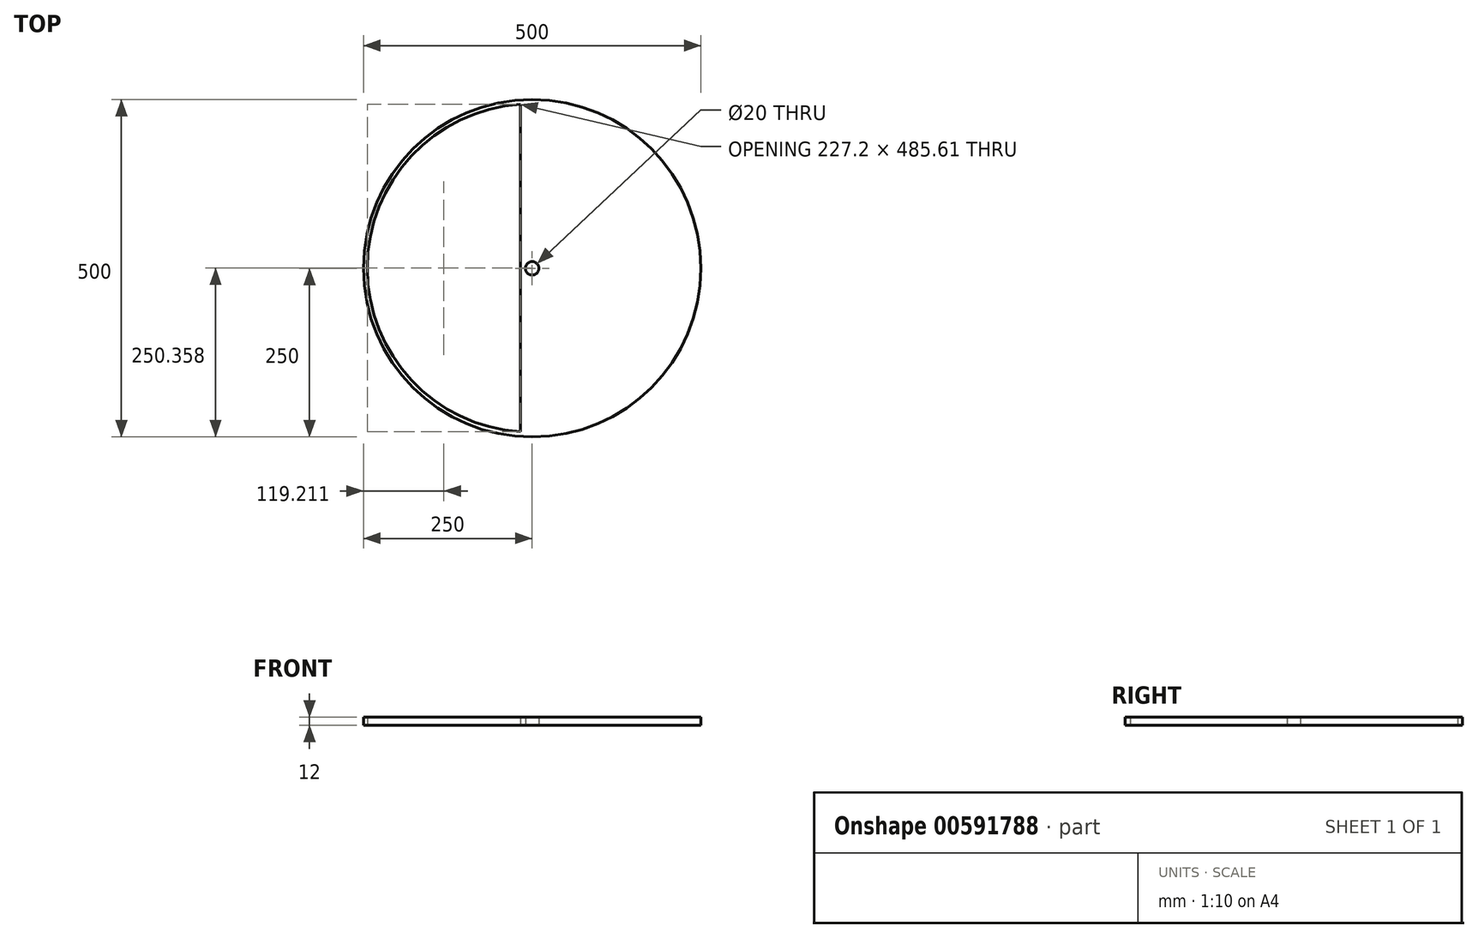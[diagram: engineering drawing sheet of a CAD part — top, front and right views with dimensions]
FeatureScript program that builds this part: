
annotation { "Feature Type Name" : "Feature", "Feature Type Description" : "" }
export const myFeature = defineFeature(function(context is Context, id is Id, definition is map)
    precondition{}
    {
        {
            var Q0;
            Q0=qCreatedBy(makeId("Top.planeOp"),FACE);
            var sketch = newSketch(context, id + "F0", { "sketchPlane" : qUnion([Q0])});
            skCircle(sketch, "E0", {"center": v(0, 0) * mm, "radius": 250 * mm});
            skSolve(sketch);
        }
        {
            var Q0;
            Q0=qSketchRegion(id+"F0",true);
            extrude(context, id + "F1", {"entities" : qUnion([Q0]), "depth" : 12 * mm});
        }
        {
            var Q0;
            Q0=qCreatedBy(makeId("Top.planeOp"),FACE);
            var sketch = newSketch(context, id + "F2", { "sketchPlane" : qUnion([Q0])});
            skCircle(sketch, "E1", {"center": v(0, 0) * mm, "radius": 10 * mm});
            skSolve(sketch);
        }
        {
            var Q0;
            Q0=qSketchRegion(id+"F2",true);
            extrude(context, id + "F3", {"entities" : qUnion([Q0]), "operationType" : NewBodyOperationType.REMOVE, "depth" : 12 * mm});
        }
        {
            var Q0;
            Q0=qCreatedBy(makeId("Top.planeOp"),FACE);
            var sketch = newSketch(context, id + "F4", { "sketchPlane" : qUnion([Q0])});
            skLineSegment(sketch, "E2", {"start": v(-17.19, 0) * mm, "end": v(-17.19, 243.16) * mm});
            skLineSegment(sketch, "E3", {"start": v(-17.19, 243.16) * mm, "end": v(-17.19, -242.45) * mm});
            skArc(sketch, "E4", {"start": v(-17.19, 243.16) * mm, "mid": v(-244.39, 0.36) * mm, "end": v(-17.19, -242.45) * mm});
            skSolve(sketch);
        }
        {
            var Q0;
            Q0=qSketchRegion(id+"F4",true);
            extrude(context, id + "F5", {"entities" : qUnion([Q0]), "operationType" : NewBodyOperationType.REMOVE, "depth" : 12 * mm});
        }
    });
